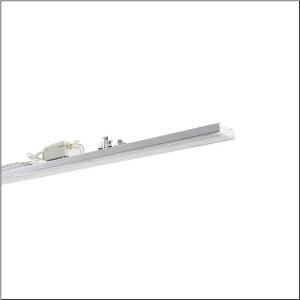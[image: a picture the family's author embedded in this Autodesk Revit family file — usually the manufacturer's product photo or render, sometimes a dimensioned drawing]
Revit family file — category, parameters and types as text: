
# Revit family: licross_r__21_recessed_mo_52tl1e7n485g_8290
name_source: partatom
category: Lighting Fixtures
units: mm (PartAtom-declared; Revit-internal decimal feet)

## family parameters
Cut with Voids When Loaded = No
Host = Face
Light Source = No
Part Type = Normal
Room Calculation Point = No
Round Connector Dimension = Use Diameter
Shared = No

## types (1)
- Licross® 21 Recessed MO (1 x LED, 8530 lm, 47.9 W, 4000K)
    Apparent Load = 48 VA
    CIE Flux Codes = 85 95 99 100 100
    Color Rendering = 80
    Color Temperature = 4000K
    Default Elevation = 1800 mm
    Description = Licross® 21 Recessed MO, luminaire insert, of sheet steel, galvanised, coil coated, white, length: 1.500mm, width: 66mm, height: 67mm, LED rated luminous flux: 8.530lm, light colour: 840, control gear: ON/OFF, with plug, 3-pole, with phase selection, mains connection: 220..240V, AC, 50/60Hz, rated input power: 48W, halogen-free wiring, primary light control with lens, of plastic, primary optical cover: cover, of PMMA, light emission: direct distribution, primary light characteristic: symmetric, protection rating (complete): IP40, insulation class (complete): insulation class I (protective earthing), certification: CE, ENEC, VDE, UKCA, protection symbol: D if used in an environment without relevant dust loads with corresponding accessories, impact resistance: IK06, permissible ambient temperature for indoor applications: -35..+40°C, corresponds to IFS (International Featured Standards) requirements for safety and quality in the food industry, reducing of maximum allowable ambient temperature of 5°C with ceiling mounting, LABS conformity tested according to VDMA 24364:2018-05, packaging unit: 1 piece
    Height = 58 mm
    Lamp = 1 x LED
    Lamp Light Flux = 8530 lm
    Lamp Power = 47.9 W
    Lamp count = 1
    Length = 1500 mm
    Luminous efficacy = 178 lm/W
    Manufacturer = Siteco
    ModVariant = No
    Model = 52TL1E7N485G
    Mounting Place = Ceiling
    Mounting Type = Pendant
    Number of Poles = 1
    OnlyDefault = Yes
    Power Factor = 1
    Product Name = Licross® 21 Recessed MO
    Product group = luminaire insert
    ProductGroupID = 901
    Protection Class = Protection class I
    Protection Degree = IP 40
    RLX_Detail_Level = 1
    RLX_Emergency_Light_Flux = 0 lm
    RLX_Emergency_Type = 0
    RLX_Emergency_Type_DB = No
    RlxData = <blob elided: 21001 chars, md5=834be3b2>
    Socket = socket
    Standby Power = 0 W
    System Light Flux = 8530 lm
    System Power = 48 W
    Type Comments = Product without accessories
    Type Image = l_1296930.jpg
    URL = http://relux.com
    VarID = ---
    Voltage = 0 V
    Weight = 0.00 kg
    Width = 66 mm

## geometry (parser evidence)
native form markers: Blend x4, Sweep x11
no freeform markers — native parametric forms only
